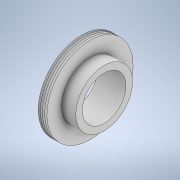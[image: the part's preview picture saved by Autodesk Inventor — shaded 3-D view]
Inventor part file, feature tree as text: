
AUTODESK INVENTOR PART (.ipt)
format: ipt  version: 2020 (Build 240168000, 168)  size: 157,696 bytes
history: native  units: mm
features: revolve x2, sketch x2, projected_geometry x1
ambient origin geometry x8: Origin, YZ Plane, XZ Plane, XY Plane, X Axis, Y Axis, Z Axis, Center Point
bodies: 实体1 (feature_tree)
feature tree (5):
  revolve  "旋转1"  [1 undecoded]
  revolve  "旋转2"  [1 undecoded]
  sketch  "草图1"  dims[d0=26.0mm d1=13.0mm]
  sketch  "草图2"  dims[d2=45.0mm d3=52.0mm d4=40.0mm d5=90.0deg d6=8.0mm d7=79.0mm d8=60.0deg d9=2.0mm d10=2.0mm d11=90.0deg]
  projected_geometry  "投影回路1"
note: 2 required parameter values undecoded (feature->parameter linkage not recoverable at this tier; creation-order binding heuristic only, values carry confidence <= 0.55)
